# Revit family: QF_BOURGEAT_tables_de_tri_hauteur_rabaissée_primaire_3TVO
name_source: partatom
category: Equipement spécialisé
revit_build: Autodesk Revit 2015 (Build: 20140606_1530(x64)
units: mm (PartAtom-declared; Revit-internal decimal feet)

## types (3) — shared parameters
Décalage du sol = 27 mm  [stored 0.0885827 ft]
Fabricant = BOURGEAT
Inox = Acier inoxydable, poli
Longueur hors tout = 1030 mm
Panneaux = PVC, non plastifié
Pieds = Oui
Spécification du Fabricant = Table de collecte et de tri hauteur rabaissée primaire
URL catalogue = http://www.bourgeat.fr

## per-type parameters (varying)
| type | Avec panneaux | Hauteur hors tout | Modèle | Poids net à vide | Poids à vide | Profondeur hors tout | Rampe |
| Sans rampe - Sans panneaux - Avec pieds | Non | 700 mm | 859003 | 41.00 kg | 41 kg | 600 mm  [stored 1.9685 ft] | Non |
| Avec rampe - Sans panneaux - Avec pieds | Non | 850 mm | 859023 | 44.00 kg | 44 kg | 850 mm | Oui |
| Avec rampe - Avec panneaux - Avec pieds | Oui | 850 mm | 859103 | 44.00 kg | 44 kg | 850 mm | Oui |

note: [stored X ft] marks values corroborated as IEEE doubles in the binary element streams (Revit-internal decimal feet)

## geometry (parser evidence)
native form markers: Blend x12
no freeform markers — native parametric forms only
